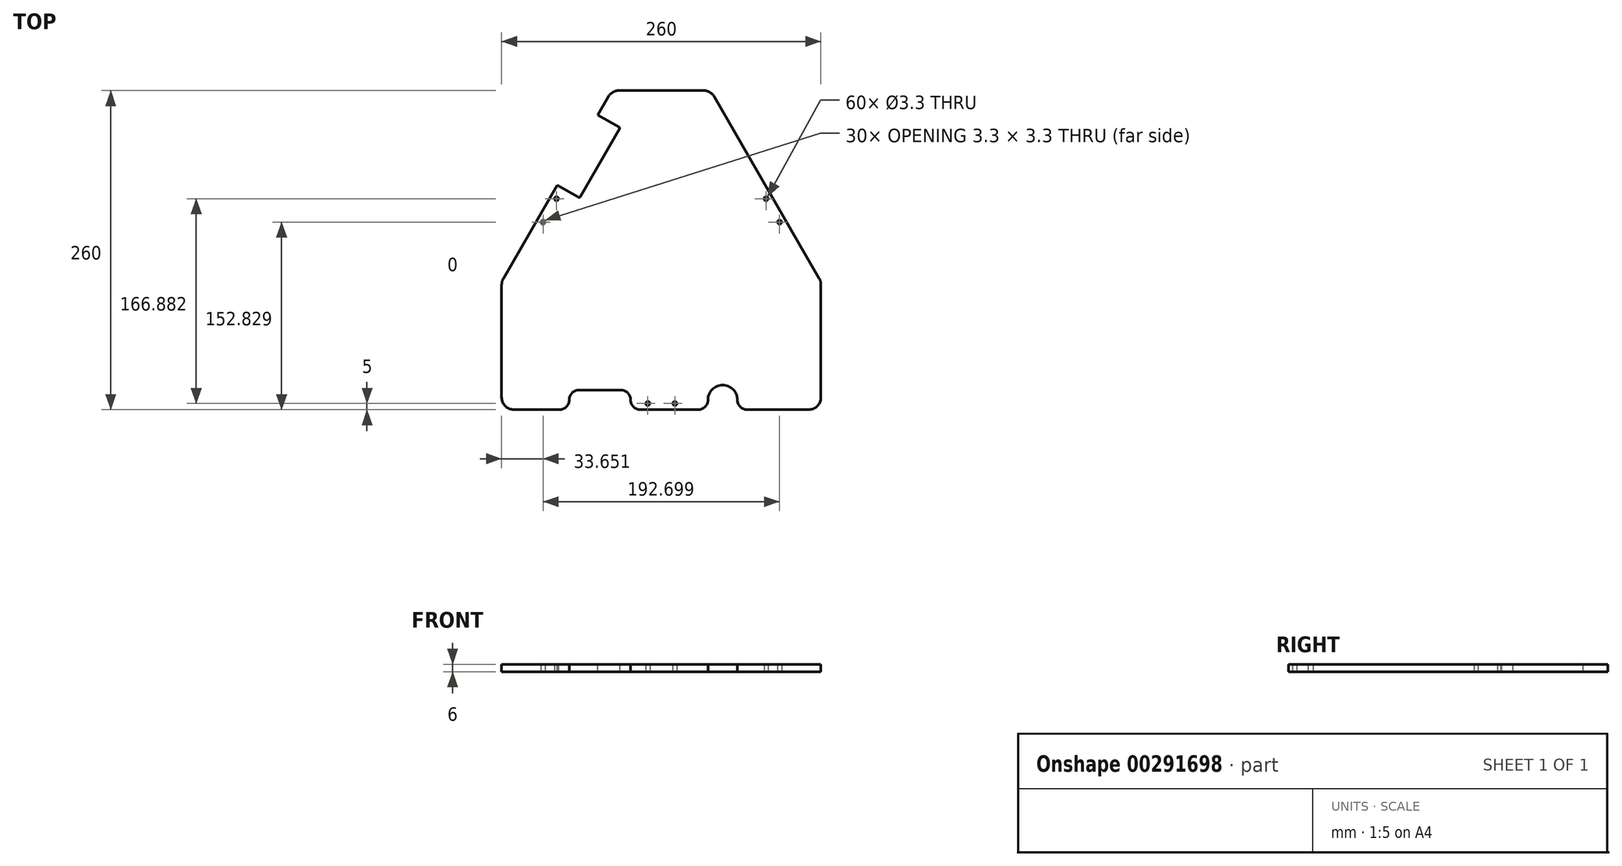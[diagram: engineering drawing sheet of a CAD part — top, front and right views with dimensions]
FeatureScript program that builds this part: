
annotation { "Feature Type Name" : "Feature", "Feature Type Description" : "" }
export const myFeature = defineFeature(function(context is Context, id is Id, definition is map)
    precondition{}
    {
        {
            var Q0;
            Q0=qCreatedBy(makeId("Top.planeOp"),FACE);
            var sketch = newSketch(context, id + "F0", { "sketchPlane" : qUnion([Q0])});
            skLineSegment(sketch, "E0", {"start": v(-225, -150) * mm, "end": v(225, -150) * mm, "construction": true});
            skLineSegment(sketch, "E1", {"start": v(-225, -150) * mm, "end": v(0, 239.71) * mm, "construction": true});
            skLineSegment(sketch, "E2", {"start": v(0, 239.71) * mm, "end": v(225, -150) * mm, "construction": true});
            skLineSegment(sketch, "E3.bottom", {"start": v(150, -150) * mm, "end": v(-150, -150) * mm, "construction": true});
            skLineSegment(sketch, "E3.top", {"start": v(150, 150) * mm, "end": v(-150, 150) * mm, "construction": true});
            skLineSegment(sketch, "E3.left", {"start": v(150, -150) * mm, "end": v(150, 150) * mm, "construction": true});
            skLineSegment(sketch, "E3.right", {"start": v(-150, -150) * mm, "end": v(-150, 150) * mm, "construction": true});
            skPoint(sketch, "E3.middle", {"position": v(0, 0) * mm});
            skLineSegment(sketch, "E4", {"start": v(130, -130) * mm, "end": v(130, -25.46) * mm});
            skLineSegment(sketch, "E5", {"start": v(130, -25.46) * mm, "end": v(40.25, 130) * mm});
            skLineSegment(sketch, "E6", {"start": v(40.25, 130) * mm, "end": v(-40.25, 130) * mm});
            skLineSegment(sketch, "E7", {"start": v(-40.25, 130) * mm, "end": v(-130, -25.46) * mm});
            skLineSegment(sketch, "E8", {"start": v(-130, -25.46) * mm, "end": v(-130, -130) * mm});
            skLineSegment(sketch, "E9", {"start": v(-130, -130) * mm, "end": v(-75, -130) * mm});
            skLineSegment(sketch, "E10", {"start": v(-75, -130) * mm, "end": v(-75, -114) * mm});
            skLineSegment(sketch, "E11", {"start": v(-75, -114) * mm, "end": v(-25, -114) * mm});
            skLineSegment(sketch, "E12", {"start": v(-25, -114) * mm, "end": v(-25, -130) * mm});
            skLineSegment(sketch, "E13", {"start": v(-25, -130) * mm, "end": v(38, -130) * mm});
            skLineSegment(sketch, "E14", {"start": v(38, -130) * mm, "end": v(38, -122) * mm});
            skLineSegment(sketch, "E15", {"start": v(130, -130) * mm, "end": v(62, -130) * mm});
            skLineSegment(sketch, "E16", {"start": v(62, -130) * mm, "end": v(62, -122) * mm});
            skArc(sketch, "E17", {"start": v(62, -122) * mm, "mid": v(50, -110) * mm, "end": v(38, -122) * mm});
            skLineSegment(sketch, "E18", {"start": v(0, 130) * mm, "end": v(0, -130) * mm, "construction": true});
            skLineSegment(sketch, "E19", {"start": v(-50, -114) * mm, "end": v(-50, -150) * mm, "construction": true});
            skLineSegment(sketch, "E20", {"start": v(50, -122) * mm, "end": v(50, -150) * mm, "construction": true});
            skSolve(sketch);
        }
        {
            var Q0;
            Q0=qSketchRegion(id+"F0",true);
            extrude(context, id + "F1", {"entities" : qUnion([Q0]), "depth" : 6 * mm});
        }
        {
            var Q0;
            Q0=makeQuery(id+"F1.opExtrude","SWEPT_EDGE",EDGE,{"disambiguationData":[OSD([sQuery(id+"F0.wireOp",EDGE,"M1viM4pK-w7LR-ZA6j-VjAJ-dASlTdO4E25m"),sQuery(id+"F0.wireOp",EDGE,"E4")])]});
            var Q1;
            Q1=makeQuery(id+"F1.opExtrude","SWEPT_EDGE",EDGE,{"disambiguationData":[OSD([sQuery(id+"F0.wireOp",EDGE,"E4"),sQuery(id+"F0.wireOp",EDGE,"E5")])]});
            var Q2;
            Q2=makeQuery(id+"F1.opExtrude","SWEPT_EDGE",EDGE,{"disambiguationData":[OSD([sQuery(id+"F0.wireOp",EDGE,"E5"),sQuery(id+"F0.wireOp",EDGE,"E6")])]});
            var Q3;
            Q3=makeQuery(id+"F1.opExtrude","SWEPT_EDGE",EDGE,{"disambiguationData":[OSD([sQuery(id+"F0.wireOp",EDGE,"E6"),sQuery(id+"F0.wireOp",EDGE,"E7")])]});
            var Q4;
            Q4=makeQuery(id+"F1.opExtrude","SWEPT_EDGE",EDGE,{"disambiguationData":[OSD([sQuery(id+"F0.wireOp",EDGE,"E7"),sQuery(id+"F0.wireOp",EDGE,"E8")])]});
            var Q5;
            Q5=makeQuery(id+"F1.opExtrude","SWEPT_EDGE",EDGE,{"disambiguationData":[OSD([sQuery(id+"F0.wireOp",EDGE,"M1viM4pK-w7LR-ZA6j-VjAJ-dASlTdO4E25m"),sQuery(id+"F0.wireOp",EDGE,"E8")])]});
            fillet(context, id + "F2", {"entities" : qUnion([Q0, Q1, Q2, Q3, Q4, Q5]), "radius" : 10 * mm, "tangentPropagation" : true, "allowEdgeOverflow" : false});
        }
        {
            var Q0;
            Q0=makeQuery(id+"F1.opExtrude","SWEPT_EDGE",EDGE,{"disambiguationData":[OSD([sQuery(id+"F0.wireOp",EDGE,"E9"),sQuery(id+"F0.wireOp",EDGE,"E10")])]});
            var Q1;
            Q1=makeQuery(id+"F1.opExtrude","SWEPT_EDGE",EDGE,{"disambiguationData":[OSD([sQuery(id+"F0.wireOp",EDGE,"E10"),sQuery(id+"F0.wireOp",EDGE,"E11")])]});
            var Q2;
            Q2=makeQuery(id+"F1.opExtrude","SWEPT_EDGE",EDGE,{"disambiguationData":[OSD([sQuery(id+"F0.wireOp",EDGE,"E11"),sQuery(id+"F0.wireOp",EDGE,"E12")])]});
            var Q3;
            Q3=makeQuery(id+"F1.opExtrude","SWEPT_EDGE",EDGE,{"disambiguationData":[OSD([sQuery(id+"F0.wireOp",EDGE,"E12"),sQuery(id+"F0.wireOp",EDGE,"E13")])]});
            var Q4;
            Q4=makeQuery(id+"F1.opExtrude","SWEPT_EDGE",EDGE,{"disambiguationData":[OSD([sQuery(id+"F0.wireOp",EDGE,"E13"),sQuery(id+"F0.wireOp",EDGE,"E14")])]});
            var Q5;
            Q5=makeQuery(id+"F1.opExtrude","SWEPT_EDGE",EDGE,{"disambiguationData":[OSD([sQuery(id+"F0.wireOp",EDGE,"E15"),sQuery(id+"F0.wireOp",EDGE,"E16")])]});
            fillet(context, id + "F3", {"entities" : qUnion([Q0, Q1, Q2, Q3, Q4, Q5]), "radius" : 8 * mm, "tangentPropagation" : true, "allowEdgeOverflow" : false});
        }
        {
            var Q0;
            Q0=makeQuery(id+"F1.opExtrude","CAP_FACE",FACE,{"disambiguationData":[OSD([sQuery(id+"F0.wireOp",EDGE,"E4"),sQuery(id+"F0.wireOp",EDGE,"E5"),sQuery(id+"F0.wireOp",EDGE,"E6"),sQuery(id+"F0.wireOp",EDGE,"E7"),sQuery(id+"F0.wireOp",EDGE,"E8"),sQuery(id+"F0.wireOp",EDGE,"E9"),sQuery(id+"F0.wireOp",EDGE,"E10"),sQuery(id+"F0.wireOp",EDGE,"E11"),sQuery(id+"F0.wireOp",EDGE,"E12"),sQuery(id+"F0.wireOp",EDGE,"E13"),sQuery(id+"F0.wireOp",EDGE,"E14"),sQuery(id+"F0.wireOp",EDGE,"E15"),sQuery(id+"F0.wireOp",EDGE,"E16"),sQuery(id+"F0.wireOp",EDGE,"E17")])],"isStart":false});
            var sketch = newSketch(context, id + "F4", { "sketchPlane" : qUnion([Q0])});
            skLineSegment(sketch, "E21", {"start": v(0, -20.1) * mm, "end": v(0, -130) * mm, "construction": true});
            skLineSegment(sketch, "E22", {"start": v(-95.18, 34.86) * mm, "end": v(0, -20.1) * mm, "construction": true});
            skLineSegment(sketch, "E23", {"start": v(95.18, 34.86) * mm, "end": v(0, -20.1) * mm, "construction": true});
            skPoint(sketch, "E24", {"position": v(11, -125) * mm});
            skPoint(sketch, "E25", {"position": v(-11, -125) * mm});
            skPoint(sketch, "E26.1.0", {"position": v(85.35, 41.88) * mm});
            skPoint(sketch, "E26.1.1", {"position": v(96.35, 22.83) * mm});
            skPoint(sketch, "E26.2.0", {"position": v(-96.35, 22.83) * mm});
            skPoint(sketch, "E26.2.1", {"position": v(-85.35, 41.88) * mm});
            skPoint(sketch, "E26.center", {"position": v(0, -20.1) * mm});
            skLineSegment(sketch, "E27", {"start": v(-84.68, 53.04) * mm, "end": v(-51.68, 110.2) * mm});
            skLineSegment(sketch, "E28", {"start": v(-51.68, 110.2) * mm, "end": v(-33.5, 99.7) * mm});
            skLineSegment(sketch, "E29", {"start": v(-33.5, 99.7) * mm, "end": v(-66.5, 42.54) * mm});
            skLineSegment(sketch, "E30", {"start": v(-66.5, 42.54) * mm, "end": v(-84.68, 53.04) * mm});
            skSolve(sketch);
        }
        {
            var Q0;
            Q0=sQuery(id+"F4.wireOp",VERTEX,"E24");
            var Q1;
            Q1=sQuery(id+"F4.wireOp",VERTEX,"E25");
            var Q2;
            Q2=sQuery(id+"F4.wireOp",VERTEX,"E26.2.0");
            var Q3;
            Q3=sQuery(id+"F4.wireOp",VERTEX,"E26.2.1");
            var Q4;
            Q4=sQuery(id+"F4.wireOp",VERTEX,"E26.1.1");
            var Q5;
            Q5=sQuery(id+"F4.wireOp",VERTEX,"E26.1.0");
            var Q6;
            Q6=makeQuery(id+"F1.opExtrude","SWEPT_BODY",BODY,{"disambiguationData":[OSD([sQuery(id+"F0.wireOp",EDGE,"E4"),sQuery(id+"F0.wireOp",EDGE,"E5"),sQuery(id+"F0.wireOp",EDGE,"E6"),sQuery(id+"F0.wireOp",EDGE,"E7"),sQuery(id+"F0.wireOp",EDGE,"E8"),sQuery(id+"F0.wireOp",EDGE,"E9"),sQuery(id+"F0.wireOp",EDGE,"E10"),sQuery(id+"F0.wireOp",EDGE,"E11"),sQuery(id+"F0.wireOp",EDGE,"E12"),sQuery(id+"F0.wireOp",EDGE,"E13"),sQuery(id+"F0.wireOp",EDGE,"E14"),sQuery(id+"F0.wireOp",EDGE,"E15"),sQuery(id+"F0.wireOp",EDGE,"E16"),sQuery(id+"F0.wireOp",EDGE,"E17")])]});
            hole(context, id + "F5", {"style" : HoleStyle.SIMPLE, "endStyle" : HoleEndStyle.THROUGH, "standardTappedOrClearance" : lookupTablePath({ "standard" : "ISO", "fit" : "Normal", "size" : "M3", "type" : "Clearance" }), "standardBlindInLast" : lookupTablePath({ "fit" : "Standard", "standard" : "ISO", "size" : "M3", "type" : "Clearance" }), "holeDiameter" : 3.3 * mm, "locations" : qUnion([Q0, Q1, Q2, Q3, Q4, Q5]), "scope" : qUnion([Q6]), "isTappedThrough" : true, "startStyle" : HoleStartStyle.PART});
        }
        {
            var Q0;
            Q0=qSketchRegion(id+"F4",true);
            extrude(context, id + "F6", {"entities" : qUnion([Q0]), "operationType" : NewBodyOperationType.REMOVE, "endBound" : BoundingType.THROUGH_ALL, "oppositeDirection" : true, "depth" : 25 * mm});
        }
        {
            var Q0;
            Q0=makeQuery(id+"F6.boolean.opBoolean","COPY",EDGE,{"derivedFrom":makeQuery(id+"F6.opExtrude","SWEPT_EDGE",EDGE,{"disambiguationData":[OSD([sQuery(id+"F4.wireOp",EDGE,"E28"),sQuery(id+"F4.wireOp",EDGE,"E29")])]})});
            var Q1;
            Q1=makeQuery(id+"F6.boolean.opBoolean","COPY",EDGE,{"derivedFrom":makeQuery(id+"F6.opExtrude","SWEPT_EDGE",EDGE,{"disambiguationData":[OSD([sQuery(id+"F4.wireOp",EDGE,"E29"),sQuery(id+"F4.wireOp",EDGE,"E30")])]})});
            var Q2;
            Q2=makeQuery(id+"F6.boolean.opBoolean","COPY",EDGE,{"derivedFrom":makeQuery(id+"F6.opExtrude","SWEPT_EDGE",EDGE,{"disambiguationData":[OSD([sQuery(id+"F0.wireOp",EDGE,"E7"),sQuery(id+"F4.wireOp",EDGE,"E27"),sQuery(id+"F4.wireOp",EDGE,"E28")])]})});
            var Q3;
            Q3=makeQuery(id+"F6.boolean.opBoolean","COPY",EDGE,{"derivedFrom":makeQuery(id+"F6.opExtrude","SWEPT_EDGE",EDGE,{"disambiguationData":[OSD([sQuery(id+"F0.wireOp",EDGE,"E7"),sQuery(id+"F4.wireOp",EDGE,"E27"),sQuery(id+"F4.wireOp",EDGE,"E30")])]})});
            fillet(context, id + "F7", {"entities" : qUnion([Q0, Q1, Q2, Q3]), "radius" : 1 * mm, "tangentPropagation" : true, "allowEdgeOverflow" : false});
        }
    });
